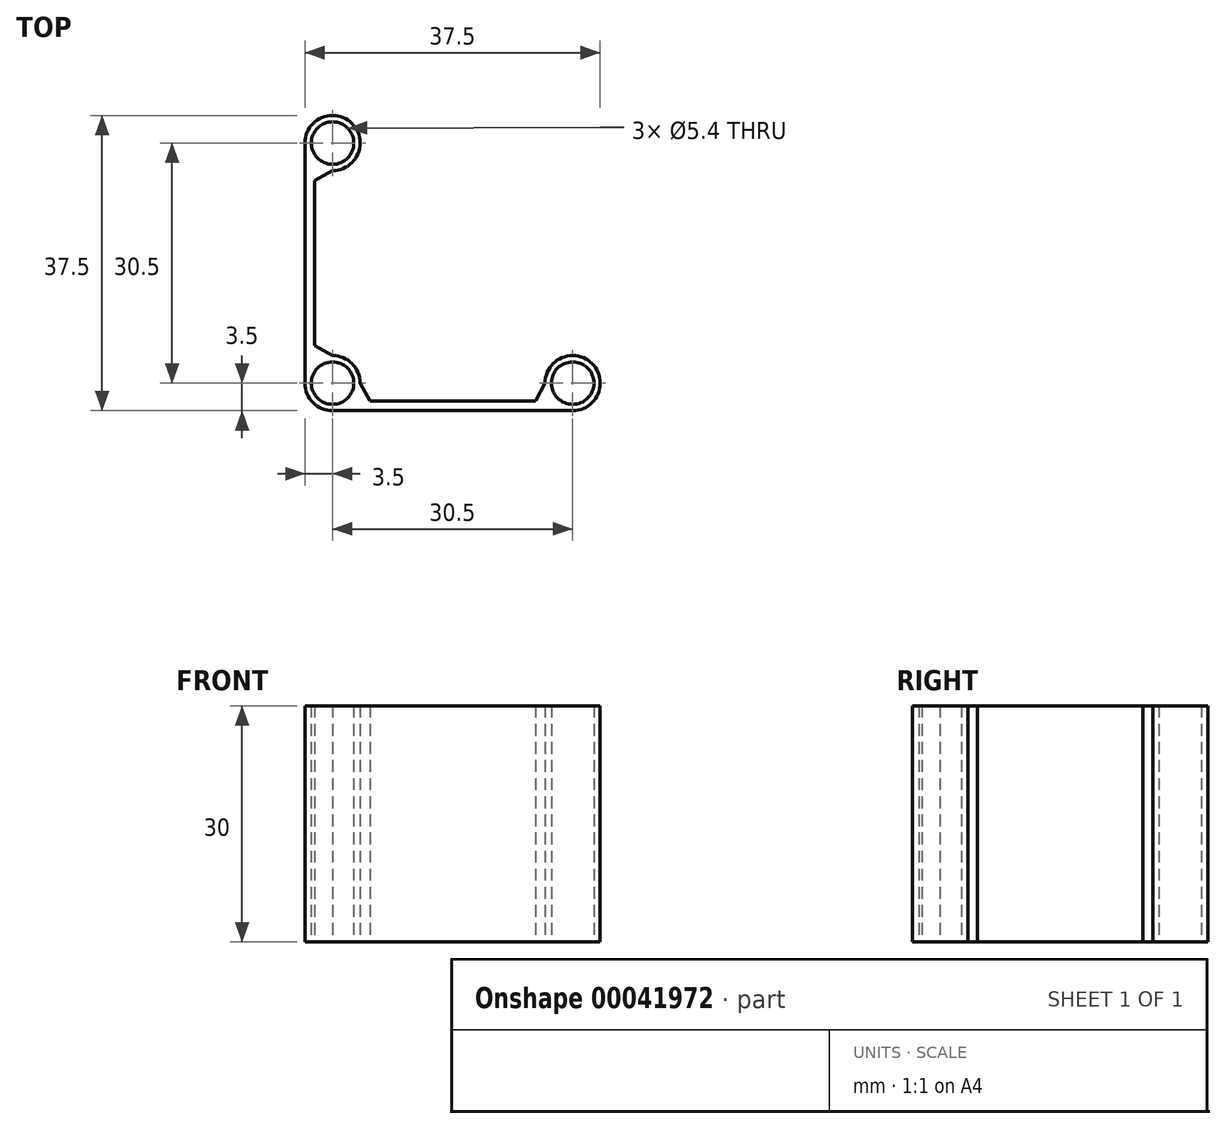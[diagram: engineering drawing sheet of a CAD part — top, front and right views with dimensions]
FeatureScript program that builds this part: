
annotation { "Feature Type Name" : "Feature", "Feature Type Description" : "" }
export const myFeature = defineFeature(function(context is Context, id is Id, definition is map)
    precondition{}
    {
        {
            var Q0;
            Q0=qCreatedBy(makeId("Top.planeOp"),FACE);
            var sketch = newSketch(context, id + "F0", { "sketchPlane" : qUnion([Q0])});
            skLineSegment(sketch, "E0.rect.bottom", {"start": v(15.25, -15.25) * mm, "end": v(-15.25, -15.25) * mm, "construction": true});
            skLineSegment(sketch, "E0.rect.top", {"start": v(15.25, 15.25) * mm, "end": v(-15.25, 15.25) * mm, "construction": true});
            skLineSegment(sketch, "E0.rect.left", {"start": v(15.25, -15.25) * mm, "end": v(15.25, 15.25) * mm, "construction": true});
            skLineSegment(sketch, "E0.rect.right", {"start": v(-15.25, -15.25) * mm, "end": v(-15.25, 15.25) * mm, "construction": true});
            skPoint(sketch, "E0.rect.middle", {"position": v(0, 0) * mm});
            skCircle(sketch, "E1", {"center": v(-15.25, 15.25) * mm, "radius": 2.7 * mm});
            skCircle(sketch, "E2", {"center": v(-15.25, -15.25) * mm, "radius": 2.7 * mm});
            skCircle(sketch, "E3", {"center": v(15.25, -15.25) * mm, "radius": 2.7 * mm});
            skCircle(sketch, "E4", {"center": v(-15.25, 15.25) * mm, "radius": 3.5 * mm});
            skCircle(sketch, "E5", {"center": v(-15.25, -15.25) * mm, "radius": 3.5 * mm});
            skCircle(sketch, "E6", {"center": v(15.25, -15.25) * mm, "radius": 3.5 * mm});
            skLineSegment(sketch, "E7", {"start": v(15.25, -18.75) * mm, "end": v(-15.25, -18.75) * mm});
            skLineSegment(sketch, "E8", {"start": v(-18.75, -15.25) * mm, "end": v(-18.75, 15.25) * mm});
            skLineSegment(sketch, "E9", {"start": v(-17.55, 12.61) * mm, "end": v(-17.55, -12.61) * mm});
            skLineSegment(sketch, "E10", {"start": v(-12.61, -17.55) * mm, "end": v(12.61, -17.55) * mm});
            skLineSegment(sketch, "E11", {"start": v(-15.25, -11.75) * mm, "end": v(-17.55, -10.5) * mm});
            skLineSegment(sketch, "E12", {"start": v(-15.25, 11.75) * mm, "end": v(-17.55, 10.5) * mm});
            skLineSegment(sketch, "E13", {"start": v(-11.75, -15.25) * mm, "end": v(-10.5, -17.55) * mm});
            skLineSegment(sketch, "E14", {"start": v(11.75, -15.25) * mm, "end": v(10.5, -17.55) * mm});
            skSolve(sketch);
        }
        {
            var Q0;
            Q0=makeQuery(id+"F0.imprint","IMPRINT",FACE,{"disambiguationData":[TD([[makeQuery(id+"F0.imprint","IMPRINT",EDGE,{"derivedFrom":sQuery(id+"F0.wireOp",EDGE,"E1")}),-1.0]])]});
            var Q1;
            {var subQ0=sQuery(id+"F0.wireOp",EDGE,"E12");Q1=makeQuery(id+"F0.imprint","IMPRINT",FACE,{"disambiguationData":[TD([[makeQuery(id+"F0.imprint","IMPRINT",EDGE,{"derivedFrom":subQ0}),-1.0]])]});}
            var Q2;
            {var subQ7=sQuery(id+"F0.wireOp",EDGE,"E8");Q2=makeQuery(id+"F0.imprint","IMPRINT",FACE,{"disambiguationData":[TD([[makeQuery(id+"F0.imprint","IMPRINT",EDGE,{"derivedFrom":subQ7}),-1.0]])]});}
            var Q3;
            Q3=makeQuery(id+"F0.imprint","IMPRINT",FACE,{"disambiguationData":[TD([[makeQuery(id+"F0.imprint","IMPRINT",EDGE,{"derivedFrom":sQuery(id+"F0.wireOp",EDGE,"E2")}),-1.0]])]});
            var Q4;
            {var subQ0=sQuery(id+"F0.wireOp",EDGE,"E11");Q4=makeQuery(id+"F0.imprint","IMPRINT",FACE,{"disambiguationData":[TD([[makeQuery(id+"F0.imprint","IMPRINT",EDGE,{"derivedFrom":subQ0}),1.0]])]});}
            var Q5;
            {var subQ1=sQuery(id+"F0.wireOp",EDGE,"E13");Q5=makeQuery(id+"F0.imprint","IMPRINT",FACE,{"disambiguationData":[TD([[makeQuery(id+"F0.imprint","IMPRINT",EDGE,{"derivedFrom":subQ1}),-1.0]])]});}
            var Q6;
            {var subQ7=sQuery(id+"F0.wireOp",EDGE,"E7");Q6=makeQuery(id+"F0.imprint","IMPRINT",FACE,{"disambiguationData":[TD([[makeQuery(id+"F0.imprint","IMPRINT",EDGE,{"derivedFrom":subQ7}),-1.0]])]});}
            var Q7;
            {var subQ0=sQuery(id+"F0.wireOp",EDGE,"E14");Q7=makeQuery(id+"F0.imprint","IMPRINT",FACE,{"disambiguationData":[TD([[makeQuery(id+"F0.imprint","IMPRINT",EDGE,{"derivedFrom":subQ0}),1.0]])]});}
            var Q8;
            Q8=makeQuery(id+"F0.imprint","IMPRINT",FACE,{"disambiguationData":[TD([[makeQuery(id+"F0.imprint","IMPRINT",EDGE,{"derivedFrom":sQuery(id+"F0.wireOp",EDGE,"E3")}),-1.0]])]});
            extrude(context, id + "F1", {"entities" : qUnion([Q0, Q1, Q2, Q3, Q4, Q5, Q6, Q7, Q8]), "depth" : 30 * mm});
        }
    });
